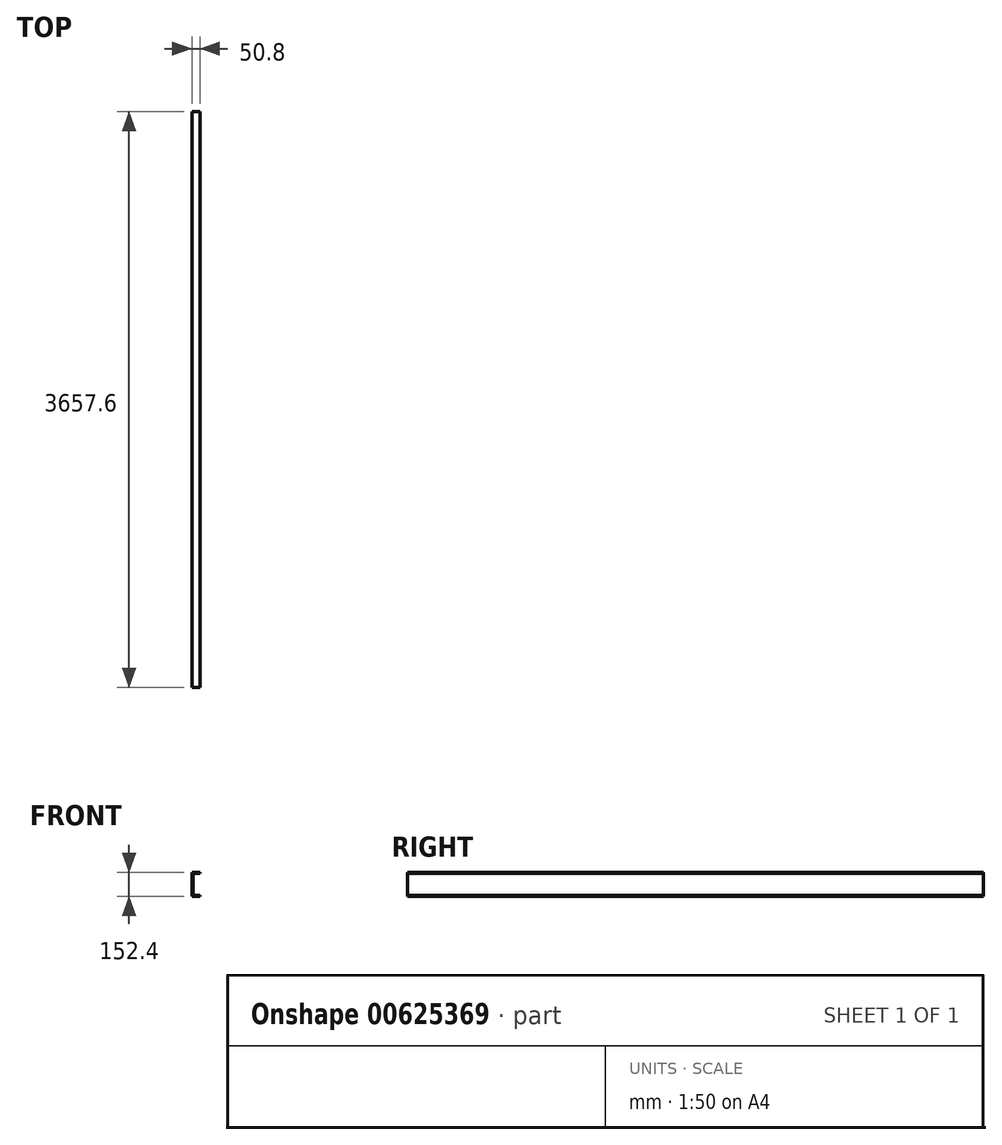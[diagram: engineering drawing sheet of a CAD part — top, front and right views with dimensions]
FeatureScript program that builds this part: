
annotation { "Feature Type Name" : "Feature", "Feature Type Description" : "" }
export const myFeature = defineFeature(function(context is Context, id is Id, definition is map)
    precondition{}
    {
        {
            var Q0;
            Q0=qCreatedBy(makeId("Front.planeOp"),FACE);
            var sketch = newSketch(context, id + "F0", { "sketchPlane" : qUnion([Q0])});
            skLineSegment(sketch, "E0.bottom", {"start": v(-25.4, 76.2) * mm, "end": v(25.4, 76.2) * mm});
            skLineSegment(sketch, "E0.top", {"start": v(-25.4, -76.2) * mm, "end": v(25.4, -76.2) * mm});
            skLineSegment(sketch, "E0.left", {"start": v(-25.4, 76.2) * mm, "end": v(-25.4, -76.2) * mm});
            skLineSegment(sketch, "E0.right", {"start": v(25.4, 76.2) * mm, "end": v(25.4, 69.85) * mm});
            skPoint(sketch, "E0.middle", {"position": v(0, 0) * mm});
            skLineSegment(sketch, "E1", {"start": v(-19.05, -69.85) * mm, "end": v(-19.05, 69.85) * mm});
            skLineSegment(sketch, "E2", {"start": v(-19.05, 69.85) * mm, "end": v(25.4, 69.85) * mm});
            skLineSegment(sketch, "E3", {"start": v(-19.05, -69.85) * mm, "end": v(25.4, -69.85) * mm});
            skLineSegment(sketch, "E4", {"start": v(25.4, -69.85) * mm, "end": v(25.4, -76.2) * mm});
            skSolve(sketch);
        }
        {
            var Q0;
            Q0=makeQuery(id+"F0.imprint","IMPRINT",FACE,{"disambiguationData":[TD([[makeQuery(id+"F0.imprint","IMPRINT",EDGE,{"derivedFrom":sQuery(id+"F0.wireOp",EDGE,"E0.bottom")}),-1.0]])]});
            extrude(context, id + "F1", {"entities" : qUnion([Q0]), "depth" : 3657.6 * mm, "offsetDistance" : 25.4 * mm});
        }
    });
